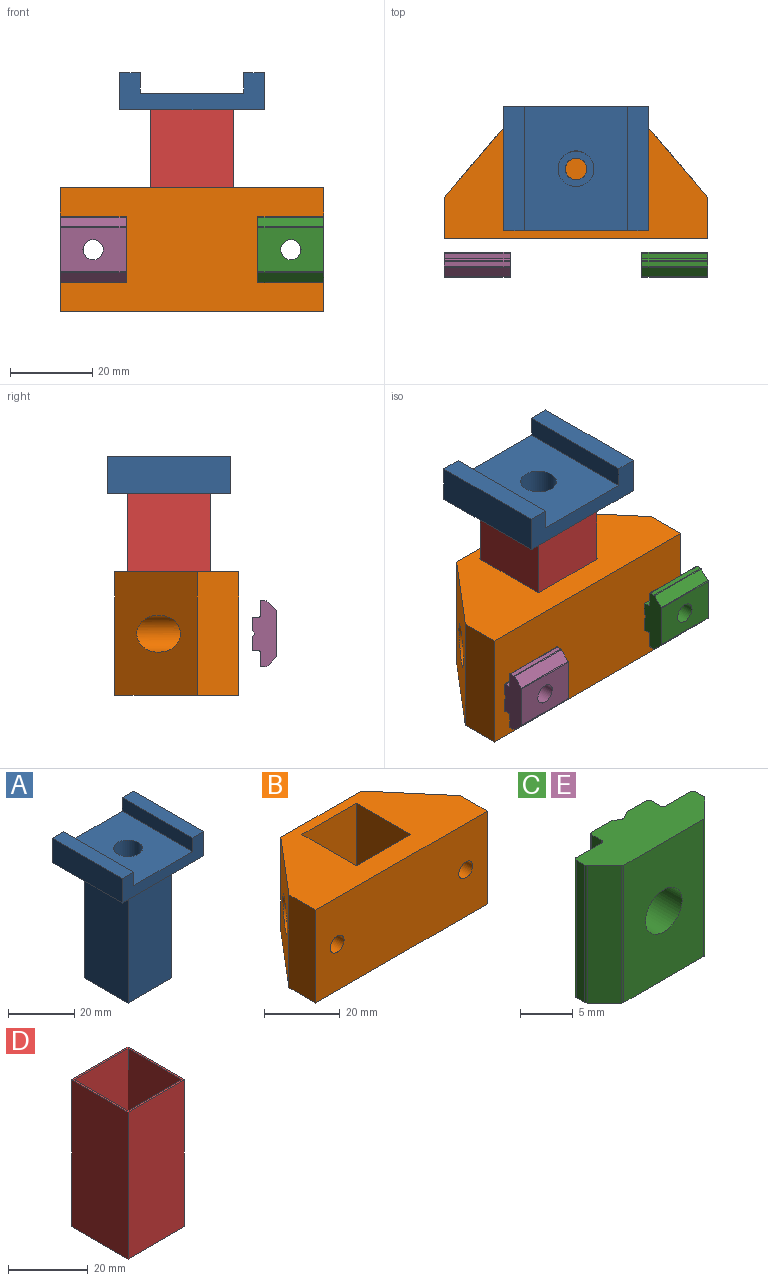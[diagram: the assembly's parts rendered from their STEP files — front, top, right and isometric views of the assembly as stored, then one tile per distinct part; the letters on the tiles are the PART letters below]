
ASSEMBLY  parts=5 mates=5
PART A: 25 faces, bbox 35x30x53 mm
  f0: cylinder r=2.6mm len=5.2mm, axis (0,0,-1), area 81.7mm2, adj f22,f24
  f1: plane 30x25.2mm, normal (0,0,1), area 696.6mm2, adj f8,f10,f12,f14,f23
  f2: plane 44x18.6mm, normal (0,-1,0), area 818.4mm2, adj f3,f5,f6,f7
  f3: plane 44x18.6mm, normal (1,0,0), area 818.4mm2, adj f2,f4,f6,f7
  f4: plane 44x18.6mm, normal (0,1,0), area 818.4mm2, adj f3,f5,f6,f7
  f5: plane 44x18.6mm, normal (-1,0,0), area 818.4mm2, adj f2,f4,f6,f7
  f6: plane 18.6x18.6mm, normal (0,0,-1), area 287.7mm2, adj f2,f3,f4,f5,f16,f17,f18,f19
  f7: plane 35x30mm, normal (0,0,-1), area 704mm2, adj f2,f3,f4,f5,f8,f9,f10,f11
  f8: plane 35x9mm, normal (0,-1,0), area 189mm2, adj f1,f7,f9,f11,f12,f13,f14,f15
  f9: plane 30x9mm, normal (1,0,0), area 270mm2, adj f7,f8,f10,f15
  f10: plane 35x9mm, normal (0,1,0), area 189mm2, adj f1,f7,f9,f11,f12,f13,f14,f15
  f11: plane 30x9mm, normal (-1,0,0), area 270mm2, adj f7,f8,f10,f13
  f12: plane 30x5mm, normal (1,0,0), area 150mm2, adj f1,f8,f10,f13
  f13: plane 30x4.9mm, normal (0,0,1), area 147mm2, adj f8,f10,f11,f12
  f14: plane 30x5mm, normal (-1,0,0), area 150mm2, adj f1,f8,f10,f15
  f15: plane 30x4.9mm, normal (0,0,1), area 147mm2, adj f8,f9,f10,f14
  f16: plane 8x4.73mm, normal (0,-1,0), area 37.9mm2, adj f6,f17,f21,f22
  f17: plane 8x4.1mm, normal (-0.87,-0.5,0), area 37.9mm2, adj f6,f16,f18,f22
  f18: plane 8x4.1mm, normal (-0.87,0.5,0), area 37.9mm2, adj f6,f17,f19,f22
  f19: plane 8x4.73mm, normal (0,1,0), area 37.9mm2, adj f6,f18,f20,f22
  f20: plane 8x4.1mm, normal (0.87,0.5,0), area 37.9mm2, adj f6,f19,f21,f22
  f21: plane 8x4.1mm, normal (0.87,-0.5,0), area 37.9mm2, adj f6,f16,f20,f22
  f22: plane 9.47x8.2mm, normal (0,0,-1), area 37mm2, adj f0,f16,f17,f18,f19,f20,f21
  f23: cylinder r=4.35mm len=35mm, axis (0,0,1), area 956.6mm2, adj f1,f24
  f24: plane 8.7x8.7mm, normal (0,0,1), area 38.2mm2, adj f0,f23
PART B: 19 faces, bbox 66.2x32.2x32.2 mm
  f0: plane 64x30mm, normal (0,-1,0), area 1877.5mm2, adj f1,f2,f6,f7,f13,f14
  f1: plane 64x30mm, normal (0,0,1), area 1172mm2, adj f0,f2,f3,f4,f5,f6,f8,f9
  f2: plane 30x10mm, normal (1,0,0), area 300mm2, adj f0,f1,f3,f7
  f3: plane 32.23x22.23mm, normal (0.76,0.65,0), area 689.2mm2, adj f1,f2,f4,f7,f15
  f4: plane 30x30mm, normal (0,1,0), area 900mm2, adj f1,f3,f5,f7
  f5: plane 32.23x22.23mm, normal (-0.76,0.65,0), area 689.2mm2, adj f1,f4,f6,f7,f17
  f6: plane 30x10mm, normal (-1,0,0), area 300mm2, adj f0,f1,f5,f7
  f7: plane 64x30mm, normal (0,0,-1), area 1580mm2, adj f0,f2,f3,f4,f5,f6
  f8: plane 26x20.2mm, normal (0,1,0), area 525.2mm2, adj f1,f9,f11,f12
  f9: plane 26x20.2mm, normal (-1,0,0), area 525.2mm2, adj f1,f8,f10,f12
  f10: plane 26x20.2mm, normal (0,-1,0), area 525.2mm2, adj f1,f9,f11,f12
  f11: plane 26x20.2mm, normal (1,0,0), area 525.2mm2, adj f1,f8,f10,f12
  f12: plane 20.2x20.2mm, normal (0,0,1), area 408mm2, adj f8,f9,f10,f11
  f13: cylinder r=2.6mm len=12mm, axis (0,-1,0), area 196mm2, adj f0,f18
  f14: cylinder r=2.6mm len=12mm, axis (0,-1,0), area 196mm2, adj f0,f16
  f15: cylinder r=4.5mm len=12.73mm, axis (0,-1,0), area 214.7mm2, adj f3,f16
  f16: plane 9x9mm, normal (0,1,0), area 42.4mm2, adj f14,f15
  f17: cylinder r=4.5mm len=12.73mm, axis (0,-1,0), area 214.7mm2, adj f5,f18
  f18: plane 9x9mm, normal (0,1,0), area 42.4mm2, adj f13,f17
PART C: 30 faces, bbox 16x6x16 mm
  f0: plane 16x6mm, normal (0,0,-1), area 73.9mm2, adj f1,f2,f3,f4,f5,f6,f7,f8
  f1: cylinder r=0.3mm len=16mm, axis (0,0,1), area 3.8mm2, adj f0,f2,f12,f13
  f2: plane 16x1.18mm, normal (-1,0,0), area 18.8mm2, adj f0,f1,f3,f13
  f3: cylinder r=0.3mm len=16mm, axis (0,0,1), area 7.5mm2, adj f0,f2,f4,f13
  f4: plane 16x3.4mm, normal (0,1,0), area 54.4mm2, adj f0,f3,f5,f13
  f5: cylinder r=0.3mm len=16mm, axis (0,0,1), area 7.5mm2, adj f0,f4,f6,f13
  f6: plane 16x1.3mm, normal (-1,0,0), area 20.8mm2, adj f0,f5,f7,f13
  f7: cylinder r=0.3mm len=16mm, axis (0,0,1), area 7.5mm2, adj f0,f6,f8,f13
  f8: plane 16x2.7mm, normal (0,1,0), area 38.5mm2, adj f0,f7,f9,f13,f14,f15
  f9: cylinder r=2.46mm len=6mm, axis (0,-1,0), area 91.6mm2, adj f8,f10,f14,f15,f16,f17,f18,f19
  f10: plane 16x10.75mm, normal (0,-1,0), area 153mm2, adj f0,f9,f11,f13,f29
  f11: cylinder r=0.3mm len=16mm, axis (0,0,1), area 3.8mm2, adj f0,f10,f12,f13
  f12: plane 16x2.32mm, normal (-0.71,-0.71,0), area 52.6mm2, adj f0,f1,f11,f13
  f13: plane 16x6mm, normal (0,0,1), area 73.9mm2, adj f1,f2,f3,f4,f5,f6,f7,f8
  f14: plane 5.76x0.86mm, normal (0.5,0.87,0), area 5.5mm2, adj f0,f8,f9,f16
  f15: plane 5.76x0.86mm, normal (0.5,0.87,0), area 5.5mm2, adj f8,f9,f13,f17
  f16: cylinder r=0.3mm len=5.54mm, axis (0,0,1), area 1.7mm2, adj f0,f9,f14,f18
  f17: cylinder r=0.3mm len=5.54mm, axis (0,0,1), area 1.7mm2, adj f9,f13,f15,f19
  f18: plane 5.76x0.86mm, normal (-0.5,0.87,0), area 5.5mm2, adj f0,f9,f16,f20
  f19: plane 5.76x0.86mm, normal (-0.5,0.87,0), area 5.5mm2, adj f9,f13,f17,f20
  f20: plane 16x2.7mm, normal (0,1,0), area 38.5mm2, adj f0,f9,f13,f18,f19,f21
  f21: cylinder r=0.3mm len=16mm, axis (0,0,1), area 7.5mm2, adj f0,f13,f20,f22
  f22: plane 16x1.3mm, normal (1,0,0), area 20.8mm2, adj f0,f13,f21,f23
  f23: cylinder r=0.3mm len=16mm, axis (0,0,1), area 7.5mm2, adj f0,f13,f22,f24
  f24: plane 16x3.4mm, normal (0,1,0), area 54.4mm2, adj f0,f13,f23,f25
  f25: cylinder r=0.3mm len=16mm, axis (0,0,1), area 7.5mm2, adj f0,f13,f24,f26
  f26: plane 16x1.18mm, normal (1,0,0), area 18.8mm2, adj f0,f13,f25,f27
  f27: cylinder r=0.3mm len=16mm, axis (0,0,1), area 3.8mm2, adj f0,f13,f26,f28
  f28: plane 16x2.32mm, normal (0.71,-0.71,0), area 52.6mm2, adj f0,f13,f27,f29
  f29: cylinder r=0.3mm len=16mm, axis (0,0,1), area 3.8mm2, adj f0,f10,f13,f28
PART D: 10 faces, bbox 20x20x45 mm
  f0: plane 45x20mm, normal (0,-1,0), area 900mm2, adj f1,f7,f8,f9
  f1: plane 45x20mm, normal (1,0,0), area 900mm2, adj f0,f2,f8,f9
  f2: plane 45x20mm, normal (0,1,0), area 900mm2, adj f1,f7,f8,f9
  f3: plane 45x19mm, normal (-1,0,0), area 855mm2, adj f4,f6,f8,f9
  f4: plane 45x19mm, normal (0,1,0), area 855mm2, adj f3,f5,f8,f9
  f5: plane 45x19mm, normal (1,0,0), area 855mm2, adj f4,f6,f8,f9
  f6: plane 45x19mm, normal (0,-1,0), area 855mm2, adj f3,f5,f8,f9
  f7: plane 45x20mm, normal (-1,0,0), area 900mm2, adj f0,f2,f8,f9
  f8: plane 20x20mm, normal (0,0,1), area 39mm2, adj f0,f1,f2,f3,f4,f5,f6,f7
  f9: plane 20x20mm, normal (0,0,-1), area 39mm2, adj f0,f1,f2,f3,f4,f5,f6,f7
PART E: same geometry as C
PLACE A t=(-33.57,-8.4,23.89)mm
PLACE B t=(-33.57,-8.4,23.89)mm fixed
PLACE C rot(axis=(0,1,0),90deg) t=(-17.57,-11.73,23.89)mm
PLACE D t=(-33.57,-8.4,23.89)mm
PLACE E rot(axis=(0,1,0),90deg) t=(-65.57,-11.73,23.89)mm
MATE slider C.f9 <-> B.f14  axis (0,1,0) through (-9.57,-11.73,23.89)mm
MATE planar E.f24 <-> C.f24  axis (0,1,0) through (-57.57,-13.63,17.89)mm
MATE slider E.f9 <-> B.f13  axis (0,-1,0) through (-57.57,-11.73,23.89)mm
MATE fastened D.f9 <-> B.f12  axis (0,0,-1) through (-43.57,-1.5,12.89)mm
MATE slider A.f0 <-> D.f9  axis (0,0,-1) through (-33.57,8.5,13.89)mm
